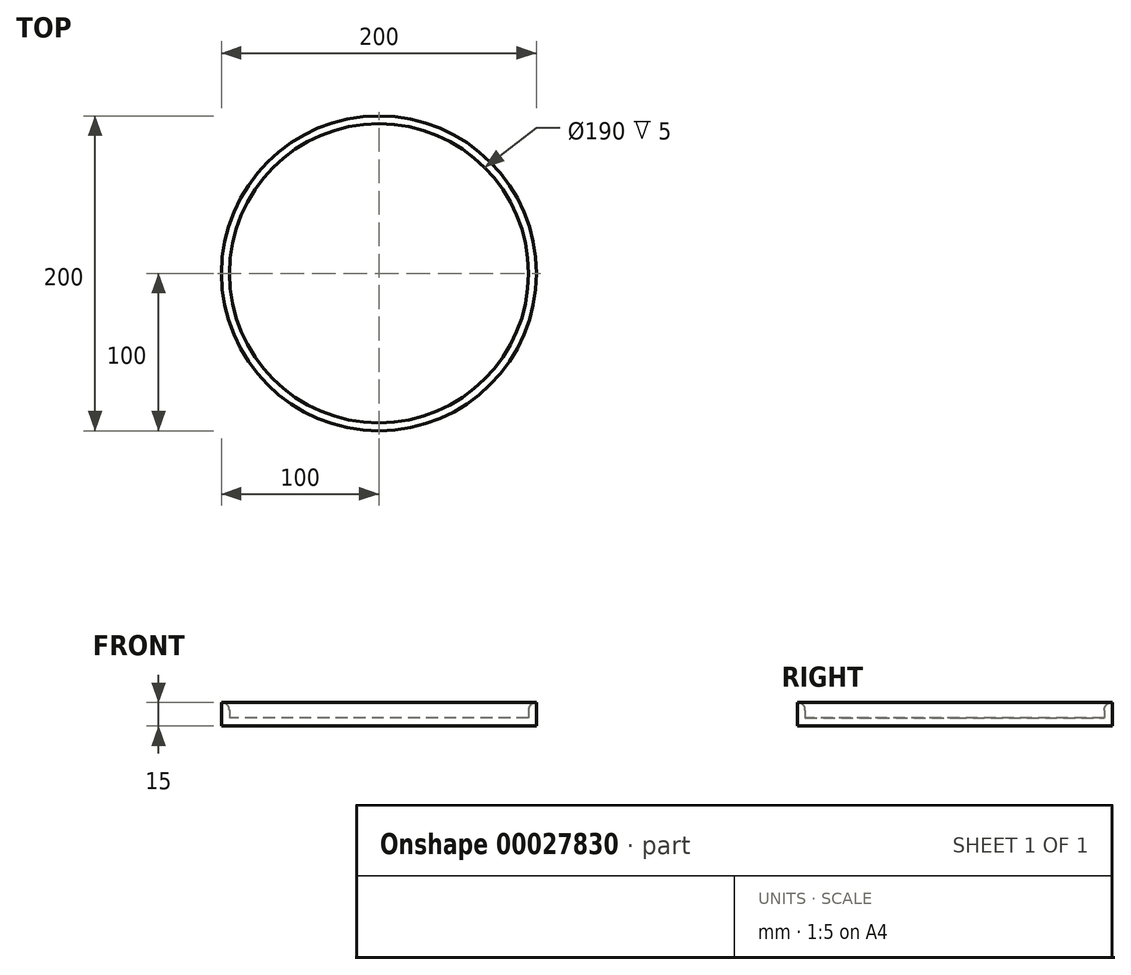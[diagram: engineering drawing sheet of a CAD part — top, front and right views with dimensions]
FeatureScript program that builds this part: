
annotation { "Feature Type Name" : "Feature", "Feature Type Description" : "" }
export const myFeature = defineFeature(function(context is Context, id is Id, definition is map)
    precondition{}
    {
        {
            var Q0;
            Q0=qCreatedBy(makeId("Top.planeOp"),FACE);
            var sketch = newSketch(context, id + "F0", { "sketchPlane" : qUnion([Q0])});
            skCircle(sketch, "E0", {"center": v(0, 0) * mm, "radius": 100 * mm});
            skSolve(sketch);
        }
        {
            var Q0;
            Q0=makeQuery(id+"F0.imprint","IMPRINT",FACE,{"disambiguationData":[TD([[makeQuery(id+"F0.imprint","IMPRINT",EDGE,{"derivedFrom":sQuery(id+"F0.wireOp",EDGE,"E0")}),1.0]])]});
            extrude(context, id + "F1", {"entities" : qUnion([Q0]), "depth" : 15 * mm});
        }
        {
            var Q0;
            Q0=makeQuery(id+"F1.opExtrude","CAP_FACE",FACE,{"disambiguationData":[OSD([sQuery(id+"F0.wireOp",EDGE,"E0")])],"isStart":false});
            shell(context, id + "F2", {"entities" : qUnion([Q0]), "thickness" : 5 * mm});
        }
        {
            var Q0;
            {var subQ0=sQuery(id+"F0.wireOp",EDGE,"E0");Q0=makeQuery(id+"F2.opShell","OFFSET_EDGE",EDGE,{"disambiguationData":[OSD([subQ0]),TDD([makeQuery(id+"F1.opExtrude","CAP_EDGE",EDGE,{"disambiguationData":[OSD([subQ0])],"isStart":false})])]});}
            fillet(context, id + "F3", {"entities" : qUnion([Q0]), "radius" : 5 * mm, "allowEdgeOverflow" : false});
        }
    });
